# Revit family: 68564ec0-99c4-4203-872d-bf3da9cb3614
name_source: partatom
category: Windows
revit_build: Autodesk Revit 2014 (Build: 20130308_1515(x64)
units: mm (PartAtom-declared; Revit-internal decimal feet)

## types (2) — shared parameters
AAMA Designation = as Specified
Air Infiltration = as Specified
Analytic Construction = <None>
Description = Western Window Aluminum Stacked Fixed Window - Series 670 Direct Set as Specified
Forced Entry Rating = as Specified
Frame Depth = 0' - 4 1/2"
Frame Design_Nail Fin = Yes
Frame Mounting Setback = 0' - 1"
Glazing Thickness = 0' - 0 7/8"
Heat Transfer Coefficient (U) = 1 BTU/(h·ft²·°F)
Keynote = as Specified
Manufacturer = Western Window Systems
Manufacturer Fax = 602-243-3119
Manufacturer Website = https://www.westernwindowsystems.com
Maximum Size = as Specified
Meets Egress = as Specified
Miami Dade Conformance = as Specified
Model = no data
Operation = Fixed Picture
Product Data = http://www.arcat.com
R = 1.0000 (h·ft²·°F)/BTU
RO Spacing_Bottom = 0' - 0"
RO Spacing_Sides = 0' - 0 1/4"
RO Spacing_Top = 0' - 0 1/4"
Sales Information = https://www.westernwindowsystems.com
Standards Conformance = as Specified
Structural Test Pressure = as Specified
Thermal Resistance (R) = 1.0000 (h·ft²·°F)/BTU
U = 1 BTU/(h·ft²·°F)
URL = https://www.westernwindowsystems.com
Wall Closure = By host
Water Penetration = as Specified
zero-valued in all types: Expected Lifespan (Years), Maintenance Schedule (Months), SHGC, STC Rating, Solar Heat Gain Coefficient, VLT, Visual Light Transmittance, Warranty Duration (Years)

## type names
- Horizontal Stack
- Vertical Stack
type visibility flags: 2 boolean params named "<type name>" — each type sets only its own to Yes (folded from table)

## geometry (parser evidence)
native form markers: Sweep x5
no freeform markers — native parametric forms only
